# Revit family: Skope BB380X
name_source: partatom
category: Specialty Equipment
revit_build: Autodesk Revit 2016 (Build: 20150714_1515(x64)
units: mm (PartAtom-declared; Revit-internal decimal feet)

## family parameters
Always vertical = Yes
Cut with Voids When Loaded = No
Part Type = Normal
Room Calculation Point = No
Round Connector Dimension = Use Diameter
Shared = No
Work Plane-Based = No

## types (4) — shared parameters
Bench Thickness = 40 mm  [stored 0.131234 ft]
Depth = 590 mm  [stored 1.9357 ft]
Door Thickness = 71 mm
Door Width = 560 mm  [stored 1.83727 ft]
DoorNo = 2
Height = 920 mm  [stored 3.01837 ft]
Interior Wheel Offset = 90 mm  [stored 0.295276 ft]
Large Unit Size = 380 mm
MH = 880 mm  [stored 2.88714 ft]
MS = 1120 mm  [stored 3.67454 ft]
MW = 519 mm
Manufacturer = Skope Ltd.
Sliding = No
Small Unit Size = 235 mm  [stored 0.770997 ft]
Swing = Yes

## per-type parameters (varying)
| type | Description | LH Refridgeration Unit | LH Unit | LHL | LHS | Large Refridgeration Unit | Model | RH Refridgeration Unit | RH Unit | RHL | RHS | Refridgeration Unit Depth | Small Refridgeration Unit | Width |
| 2 Swing Doors Chiller Integral (LH) | Horizontal, 2 door Backbar bottle Chiller with Integral, LH refrigeration services | 380 mm | Yes | Yes | No | Yes | BB380X-2SW | 0 mm  [stored 0 ft] | No | No | No | 380 mm | No | 1500 mm  [stored 4.92126 ft] |
| 2 Swing Doors Chiller Integral (RH) | Horizontal, 2 door Backbar bottle Chiller with Integral, RH refrigeration services | 0 mm  [stored 0 ft] | No | No | No | Yes | BB380X-2SW-RH | 380 mm | Yes | Yes | No | 380 mm | No | 1500 mm  [stored 4.92126 ft] |
| 2 Swing Doors Chiller Remote (LH) | Horizontal, 2 door Backbar bottle Chiller with Remote, LH refrigeration services | 235 mm  [stored 0.770997 ft] | Yes | No | Yes | No | BB380Xr-2SW | 0 mm  [stored 0 ft] | No | No | No | 235 mm  [stored 0.770997 ft] | Yes | 1355 mm  [stored 4.44554 ft] |
| 2 Swing Doors Chiller Remote (RH) | Horizontal, 2 door Backbar bottle Chiller with Remote, RH refrigeration services | 0 mm  [stored 0 ft] | No | No | No | No | BB380Xr-2SW-RH | 235 mm  [stored 0.770997 ft] | Yes | No | Yes | 235 mm  [stored 0.770997 ft] | Yes | 1355 mm  [stored 4.44554 ft] |

note: [stored X ft] marks values corroborated as IEEE doubles in the binary element streams (Revit-internal decimal feet)

## geometry (parser evidence)
native form markers: Sweep x77
no freeform markers — native parametric forms only
